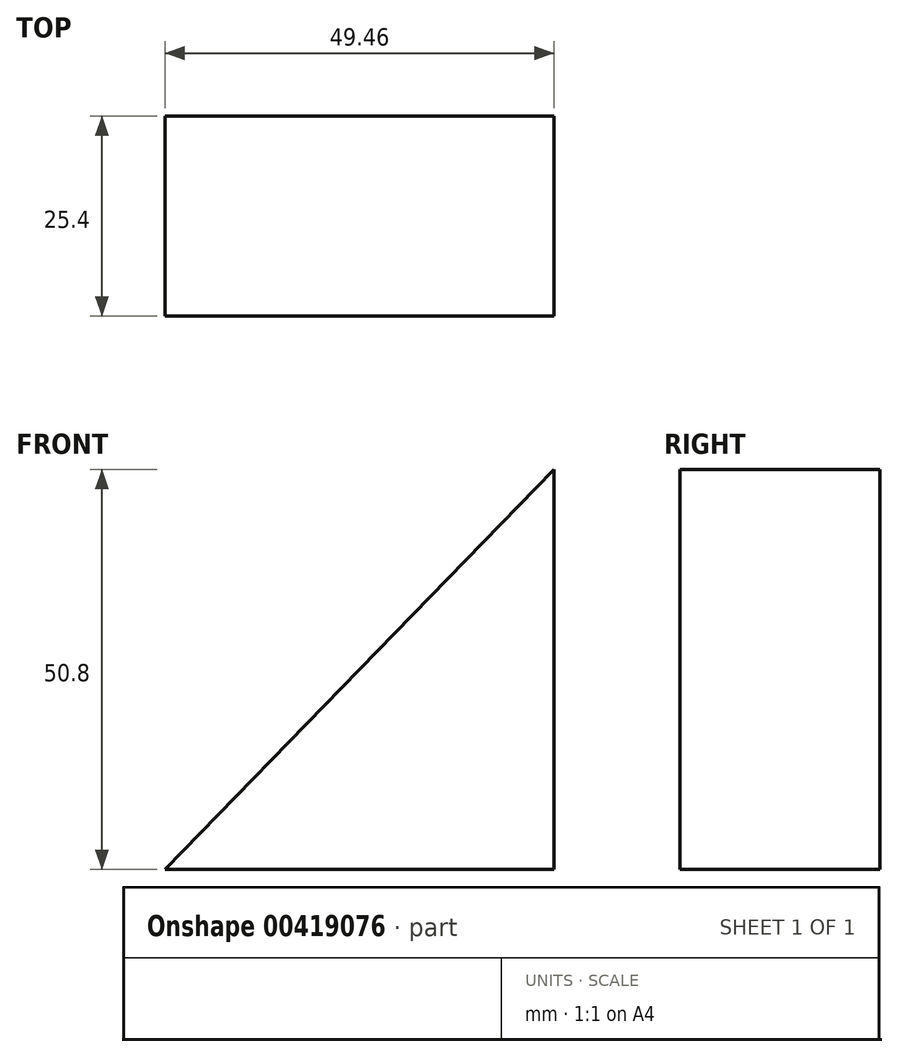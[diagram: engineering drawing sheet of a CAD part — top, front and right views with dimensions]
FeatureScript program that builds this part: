
annotation { "Feature Type Name" : "Feature", "Feature Type Description" : "" }
export const myFeature = defineFeature(function(context is Context, id is Id, definition is map)
    precondition{}
    {
        {
            var Q0;
            Q0=qCreatedBy(makeId("Front.planeOp"),FACE);
            var sketch = newSketch(context, id + "F0", { "sketchPlane" : qUnion([Q0])});
            skLineSegment(sketch, "E0", {"start": v(-50.8, 0) * mm, "end": v(0, 0) * mm});
            skLineSegment(sketch, "E1", {"start": v(0, 0) * mm, "end": v(0, 50.8) * mm});
            skLineSegment(sketch, "E2", {"start": v(0, 50.8) * mm, "end": v(-49.46, 0) * mm});
            skLineSegment(sketch, "E3", {"start": v(-49.46, 0) * mm, "end": v(-25.7, 24.4) * mm});
            skLineSegment(sketch, "E4", {"start": v(-25.7, 24.4) * mm, "end": v(0, 50.8) * mm});
            skSolve(sketch);
        }
        {
            var Q0;
            Q0 = qSketchRegion(id + "F0", true);
            extrude(context, id + "F1", {"entities" : qUnion([Q0]), "depth" : 25.4 * mm});
        }
    });
